# Revit family: Ramp_Wheelchair_American-Access_Sidekick-Folding
name_source: partatom
category: Generic Models
units: mm (PartAtom-declared; Revit-internal decimal feet)

## family parameters
Always vertical = Yes
Can host rebar = No
Cut with Voids When Loaded = No
Maintain Annotation Orientation = No
OmniClass Number = 23-17.23.11
Part Type = Normal
Room Calculation Point = No
Round Connector Dimension = Use Diameter
Shared = No
Work Plane-Based = Yes

## types (5) — shared parameters
Assembly Code = F1010200
Building Codes = http://aaramps.com
Construction Details = http://www.arcat.com
Default Elevation = 4' - 0"
Installation Phase = Modular Aluminum Ramps
Installation-Fabrication = http://www.arcat.com
Keynote = 05 51 20
Manufacturer = American Access, Inc.
Manufacturer Fax = 866-734-7267
Manufacturer Website = www.aaramps.com
OmniClass Title = Ramps
Post Material = American Access_Aluminum
Product Data = http://aaramps.com
Product Properties = http://www.arcat.com
Ramp Material = American Access_Aluminum Deck-Sidekick
Revision = R0_03-2018
Sales Information = http://aaramps.com  ---  http://aaramps.com
Send Message = http://aaramps.com
Specification = http://www.arcat.com
URL = http://www.arcat.com
Unit Width = 2' - 5"
Warranty Duration (Years) = 3
Weight Capacity = 800.00 lb/ft³
zero-valued in all types: Cost

## per-type parameters (varying)
| type | Description | Model | Unit Depth | Weight |
| SF3 | American Access Sidekick Foldable Threshold Ramp - 36 x 34 | SF3 | 3' - 0" | 18 lbs. |
| SF4 | American Access Sidekick Foldable Threshold Ramp - 48 x 34 | SF3 | 4' - 0" | 24 lbs. |
| SF5 | American Access Sidekick Foldable Threshold Ramp - 60 x 34 | SF5 | 5' - 0" | 31 lbs. |
| SF6 | American Access Sidekick Foldable Threshold Ramp - 72 x 34 | SF6 | 6' - 0" | 37 lbs. |
| SF2 | American Access Sidekick Foldable Threshold Ramp - 24 x 34 | SF2 | 2' - 0" | 12 lbs. |

## geometry (parser evidence)
native form markers: Sweep x3
no freeform markers — native parametric forms only
